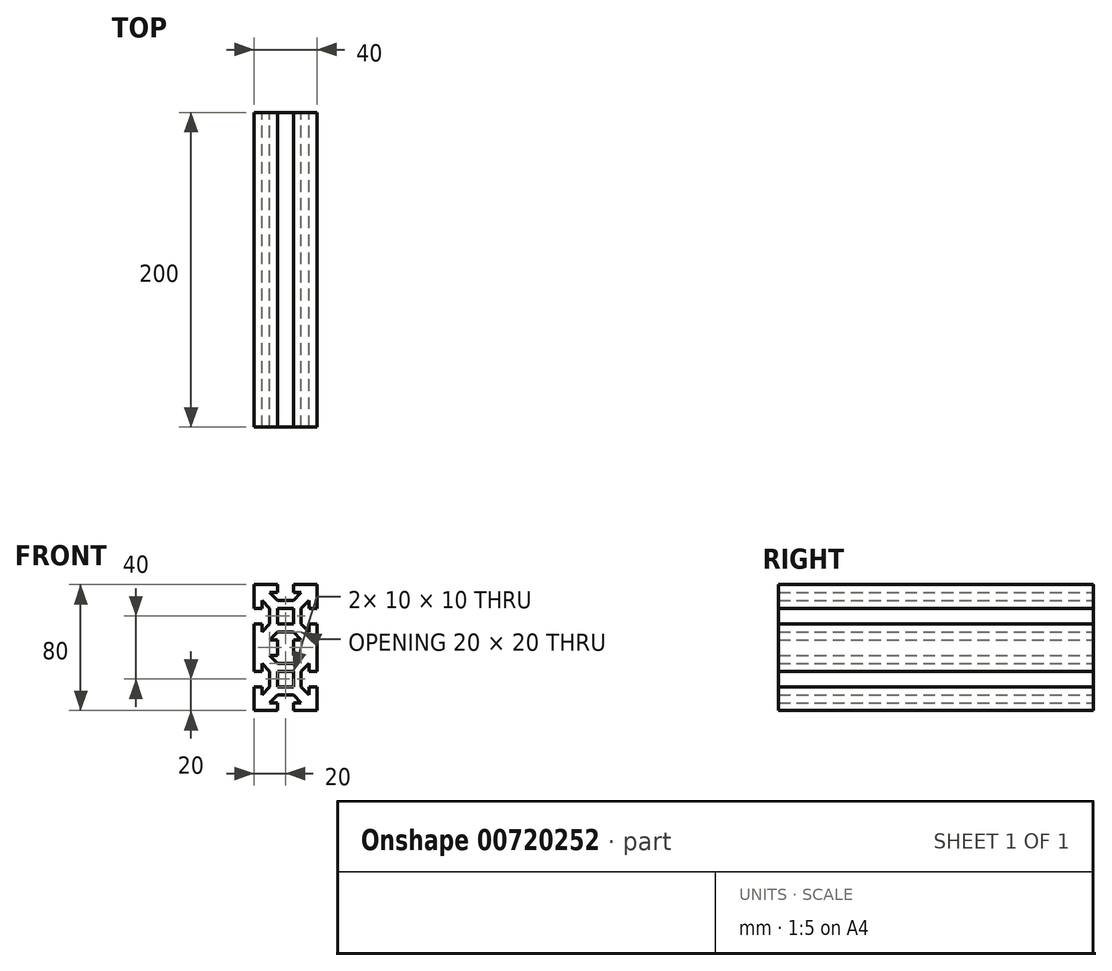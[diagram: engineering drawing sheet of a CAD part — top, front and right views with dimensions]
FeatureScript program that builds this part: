
annotation { "Feature Type Name" : "Feature", "Feature Type Description" : "" }
export const myFeature = defineFeature(function(context is Context, id is Id, definition is map)
    precondition{}
    {
        {
            var Q0;
            Q0=qCreatedBy(makeId("Front.planeOp"),FACE);
            var sketch = newSketch(context, id + "F0", { "sketchPlane" : qUnion([Q0])});
            skLineSegment(sketch, "E0.top", {"start": v(20, -20) * mm, "end": v(5, -20) * mm});
            skLineSegment(sketch, "E0.left", {"start": v(20, 20) * mm, "end": v(20, 5) * mm});
            skLineSegment(sketch, "E0.right", {"start": v(-20, 20) * mm, "end": v(-20, 5) * mm});
            skPoint(sketch, "E0.middle", {"position": v(0, 0) * mm});
            skLineSegment(sketch, "E1", {"start": v(0, 20) * mm, "end": v(0, -20) * mm, "construction": true});
            skLineSegment(sketch, "E2", {"start": v(-20, 0) * mm, "end": v(20, 0) * mm, "construction": true});
            skLineSegment(sketch, "E3", {"start": v(-20, 5) * mm, "end": v(-15, 5) * mm});
            skLineSegment(sketch, "E4", {"start": v(-20, -5) * mm, "end": v(-15, -5) * mm});
            skLineSegment(sketch, "E5", {"start": v(-5, 20) * mm, "end": v(-5, 15) * mm});
            skLineSegment(sketch, "E6", {"start": v(5, 20) * mm, "end": v(5, 15) * mm});
            skLineSegment(sketch, "E7", {"start": v(-10, 15) * mm, "end": v(-5, 15) * mm});
            skLineSegment(sketch, "E8", {"start": v(-10, -15) * mm, "end": v(-5, -15) * mm});
            skLineSegment(sketch, "E9", {"start": v(15, 10) * mm, "end": v(15, 5) * mm});
            skLineSegment(sketch, "E10", {"start": v(-15, 10) * mm, "end": v(-10, 5) * mm});
            skLineSegment(sketch, "E11", {"start": v(-10, 15) * mm, "end": v(-5, 10) * mm});
            skLineSegment(sketch, "E12", {"start": v(-15, -10) * mm, "end": v(-10, -5) * mm});
            skLineSegment(sketch, "E13", {"start": v(-10, -15) * mm, "end": v(-5, -10) * mm});
            skLineSegment(sketch, "E14.trimOffspring", {"start": v(20, -5) * mm, "end": v(20, -20) * mm});
            skLineSegment(sketch, "E15.trimOffspring", {"start": v(-20, -5) * mm, "end": v(-20, -20) * mm});
            skLineSegment(sketch, "E16.trimOffspring", {"start": v(-5, -20) * mm, "end": v(-20, -20) * mm});
            skLineSegment(sketch, "E17.trimOffspring", {"start": v(5, 15) * mm, "end": v(10, 15) * mm});
            skLineSegment(sketch, "E18.trimOffspring", {"start": v(-15, -5) * mm, "end": v(-15, -10) * mm});
            skLineSegment(sketch, "E19.trimOffspring", {"start": v(15, -5) * mm, "end": v(15, -10) * mm});
            skLineSegment(sketch, "E20.trimOffspring", {"start": v(5, -15) * mm, "end": v(10, -15) * mm});
            skLineSegment(sketch, "E21.trimOffspring", {"start": v(-5, 5) * mm, "end": v(-5, -5) * mm});
            skLineSegment(sketch, "E22.trimOffspring", {"start": v(5, 5) * mm, "end": v(5, -5) * mm});
            skLineSegment(sketch, "E23.trimOffspring", {"start": v(15, 5) * mm, "end": v(20, 5) * mm});
            skLineSegment(sketch, "E24.trimOffspring", {"start": v(15, -5) * mm, "end": v(20, -5) * mm});
            skLineSegment(sketch, "E25.trimOffspring", {"start": v(5, -15) * mm, "end": v(5, -20) * mm});
            skLineSegment(sketch, "E26.trimOffspring", {"start": v(-5, -15) * mm, "end": v(-5, -20) * mm});
            skLineSegment(sketch, "E27.trimOffspring", {"start": v(-5, -5) * mm, "end": v(5, -5) * mm});
            skLineSegment(sketch, "E28.trimOffspring", {"start": v(-5, 5) * mm, "end": v(5, 5) * mm});
            skLineSegment(sketch, "E29", {"start": v(10, 5) * mm, "end": v(10, -5) * mm});
            skLineSegment(sketch, "E30", {"start": v(-5, 10) * mm, "end": v(5, 10) * mm});
            skLineSegment(sketch, "E31", {"start": v(-10, 5) * mm, "end": v(-10, -5) * mm});
            skLineSegment(sketch, "E32", {"start": v(-5, -10) * mm, "end": v(5, -10) * mm});
            skLineSegment(sketch, "E33.trimOffspring", {"start": v(-15, 10) * mm, "end": v(-15, 5) * mm});
            skPoint(sketch, "E34.orphan", {"position": v(20, 15) * mm});
            skPoint(sketch, "E35.orphan", {"position": v(20, -15) * mm});
            skPoint(sketch, "E36.orphan", {"position": v(15, -20) * mm});
            skPoint(sketch, "E37.orphan", {"position": v(-15, -20) * mm});
            skLineSegment(sketch, "E38.trimOffspring", {"start": v(-5, 0) * mm, "end": v(0, -5) * mm});
            skLineSegment(sketch, "E39.trimOffspring", {"start": v(-5, 0) * mm, "end": v(0, 5) * mm});
            skLineSegment(sketch, "E40.trimOffspring", {"start": v(0, 5) * mm, "end": v(5, 0) * mm});
            skLineSegment(sketch, "E41.trimOffspring", {"start": v(5, 10) * mm, "end": v(10, 15) * mm});
            skLineSegment(sketch, "E42.trimOffspring", {"start": v(10, 5) * mm, "end": v(15, 10) * mm});
            skLineSegment(sketch, "E43.trimOffspring", {"start": v(10, -5) * mm, "end": v(15, -10) * mm});
            skLineSegment(sketch, "E44.trimOffspring", {"start": v(5, -10) * mm, "end": v(10, -15) * mm});
            skLineSegment(sketch, "E45.trimOffspring", {"start": v(0, -5) * mm, "end": v(5, 0) * mm});
            skLineSegment(sketch, "E46.bottom", {"start": v(20, 60) * mm, "end": v(5, 60) * mm});
            skLineSegment(sketch, "E46.left", {"start": v(20, 60) * mm, "end": v(20, 45) * mm});
            skLineSegment(sketch, "E46.right", {"start": v(-20, 60) * mm, "end": v(-20, 45) * mm});
            skPoint(sketch, "E46.middle", {"position": v(0, 40) * mm});
            skLineSegment(sketch, "E47", {"start": v(0, 60) * mm, "end": v(0, 20) * mm, "construction": true});
            skLineSegment(sketch, "E48", {"start": v(-20, 40) * mm, "end": v(20, 40) * mm, "construction": true});
            skLineSegment(sketch, "E49", {"start": v(-20, 45) * mm, "end": v(-15, 45) * mm});
            skLineSegment(sketch, "E50", {"start": v(-20, 35) * mm, "end": v(-15, 35) * mm});
            skLineSegment(sketch, "E51", {"start": v(-5, 60) * mm, "end": v(-5, 55) * mm});
            skLineSegment(sketch, "E52", {"start": v(5, 60) * mm, "end": v(5, 55) * mm});
            skLineSegment(sketch, "E53", {"start": v(-10, 55) * mm, "end": v(-5, 55) * mm});
            skLineSegment(sketch, "E54", {"start": v(-10, 25) * mm, "end": v(-5, 25) * mm});
            skLineSegment(sketch, "E55", {"start": v(15, 50) * mm, "end": v(15, 45) * mm});
            skLineSegment(sketch, "E56", {"start": v(-15, 50) * mm, "end": v(-10, 45) * mm});
            skLineSegment(sketch, "E57", {"start": v(-10, 55) * mm, "end": v(-5, 50) * mm});
            skLineSegment(sketch, "E58", {"start": v(-15, 30) * mm, "end": v(-10, 35) * mm});
            skLineSegment(sketch, "E59", {"start": v(-10, 25) * mm, "end": v(-5, 30) * mm});
            skLineSegment(sketch, "E60.trimOffspring", {"start": v(20, 35) * mm, "end": v(20, 20) * mm});
            skLineSegment(sketch, "E61.trimOffspring", {"start": v(-20, 35) * mm, "end": v(-20, 20) * mm});
            skLineSegment(sketch, "E62.trimOffspring", {"start": v(-5, 60) * mm, "end": v(-20, 60) * mm});
            skLineSegment(sketch, "E63.trimOffspring", {"start": v(5, 55) * mm, "end": v(10, 55) * mm});
            skLineSegment(sketch, "E64.trimOffspring", {"start": v(-15, 35) * mm, "end": v(-15, 30) * mm});
            skLineSegment(sketch, "E65.trimOffspring", {"start": v(15, 35) * mm, "end": v(15, 30) * mm});
            skLineSegment(sketch, "E66.trimOffspring", {"start": v(5, 25) * mm, "end": v(10, 25) * mm});
            skLineSegment(sketch, "E67.trimOffspring", {"start": v(-5, 45) * mm, "end": v(-5, 35) * mm});
            skLineSegment(sketch, "E68.trimOffspring", {"start": v(5, 45) * mm, "end": v(5, 35) * mm});
            skLineSegment(sketch, "E69.trimOffspring", {"start": v(15, 45) * mm, "end": v(20, 45) * mm});
            skLineSegment(sketch, "E70.trimOffspring", {"start": v(15, 35) * mm, "end": v(20, 35) * mm});
            skLineSegment(sketch, "E71.trimOffspring", {"start": v(5, 25) * mm, "end": v(5, 20) * mm});
            skLineSegment(sketch, "E72.trimOffspring", {"start": v(-5, 25) * mm, "end": v(-5, 20) * mm});
            skLineSegment(sketch, "E73.trimOffspring", {"start": v(-5, 35) * mm, "end": v(5, 35) * mm});
            skLineSegment(sketch, "E74.trimOffspring", {"start": v(-5, 45) * mm, "end": v(5, 45) * mm});
            skLineSegment(sketch, "E75", {"start": v(10, 45) * mm, "end": v(10, 35) * mm});
            skLineSegment(sketch, "E76", {"start": v(-5, 50) * mm, "end": v(5, 50) * mm});
            skLineSegment(sketch, "E77", {"start": v(-10, 45) * mm, "end": v(-10, 35) * mm});
            skLineSegment(sketch, "E78", {"start": v(-5, 30) * mm, "end": v(5, 30) * mm});
            skLineSegment(sketch, "E79.trimOffspring", {"start": v(-15, 50) * mm, "end": v(-15, 45) * mm});
            skPoint(sketch, "E80.orphan", {"position": v(20, 55) * mm});
            skPoint(sketch, "E81.orphan", {"position": v(20, 25) * mm});
            skPoint(sketch, "E82.orphan", {"position": v(15, 20) * mm});
            skLineSegment(sketch, "E83.trimOffspring", {"start": v(-5, 40) * mm, "end": v(0, 35) * mm});
            skLineSegment(sketch, "E84.trimOffspring", {"start": v(-5, 40) * mm, "end": v(0, 45) * mm});
            skLineSegment(sketch, "E85.trimOffspring", {"start": v(0, 45) * mm, "end": v(5, 40) * mm});
            skLineSegment(sketch, "E86.trimOffspring", {"start": v(5, 50) * mm, "end": v(10, 55) * mm});
            skLineSegment(sketch, "E87.trimOffspring", {"start": v(10, 45) * mm, "end": v(15, 50) * mm});
            skLineSegment(sketch, "E88.trimOffspring", {"start": v(10, 35) * mm, "end": v(15, 30) * mm});
            skLineSegment(sketch, "E89.trimOffspring", {"start": v(5, 30) * mm, "end": v(10, 25) * mm});
            skLineSegment(sketch, "E90.trimOffspring", {"start": v(0, 35) * mm, "end": v(5, 40) * mm});
            skSolve(sketch);
        }
        {
            var Q0;
            Q0=makeQuery(id+"F0.imprint","IMPRINT",FACE,{"disambiguationData":[TD([[makeQuery(id+"F0.imprint","IMPRINT",EDGE,{"derivedFrom":sQuery(id+"F0.wireOp",EDGE,"E0.top")}),-1.0]])]});
            extrude(context, id + "F1", {"entities" : qUnion([Q0]), "depth" : 200 * mm, "offsetDistance" : 25 * mm});
        }
    });
